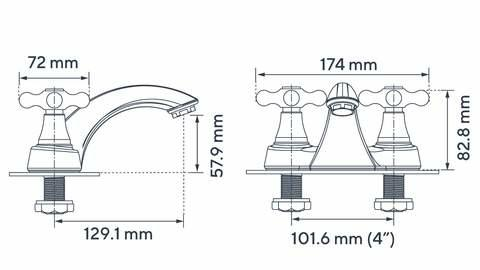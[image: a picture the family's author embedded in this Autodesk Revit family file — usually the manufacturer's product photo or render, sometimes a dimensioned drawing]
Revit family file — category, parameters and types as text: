
# Revit family: 01-0811-11 MEZCLADOR LAVAMANOS 4” CALIMA
name_source: partatom
category: Plumbing Fixtures
revit_build: Autodesk Revit 2018 (Build: 20170223_1515(x64)
units: mm (PartAtom-declared; Revit-internal decimal feet)

## family parameters
Cut with Voids When Loaded = No
Host = Face
OmniClass Number = 23.31.11.00
Part Type = Normal
Room Calculation Point = No
Round Connector Dimension = Use Diameter
Shared = No

## types (1)
- 01-0811-11
    Alto = 82.8 mm
    Alto Aireador = 57.9 mm
    CW Connection = Yes
    Default Elevation = 0 mm  [stored 0 ft]
    Description = Bimando baño
    Eje- Aireador = 129.1 mm  [stored 0.423556 ft]
    HW Connection = Yes
    Link ficha tecnica = http://infotecnica.gricol.com
    Manija = 72 mm  [stored 0.23622 ft]
    Manufacturer = Gricol
    Metal Zamak Cromado = Metal Zamak Cromado
    Model = 01-0811-11
    Plastico ABS Cromado = Plastico - ABS Cromado
    Product Name = MEZCLADOR LAVAMANOS 4” CALIMA
    Type Image = MEZCLADOR LAVAMANOS 4” CALIMA.jpg
    URL = https://www.gricol.com
    Vent Connection = No
    Waste Connection = No

note: [stored X ft] marks values corroborated as IEEE doubles in the binary element streams (Revit-internal decimal feet)

## geometry (parser evidence)
native form markers: Blend x2, Sweep x3
no freeform markers — native parametric forms only
